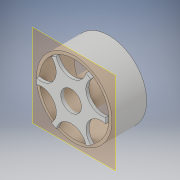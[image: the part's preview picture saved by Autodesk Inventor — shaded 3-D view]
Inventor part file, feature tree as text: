
AUTODESK INVENTOR PART (.ipt)
format: ipt  version: 2017 (Build 210142000, 142)  size: 158,720 bytes
history: native  units: in
note: dims shown in document units (in); Inventor stores cm internally (conversion verified against a paired STEP export)
features: extrude x3, sketch x3, projected_geometry x2, plane x1, pattern_circular x1
ambient origin geometry x8: Origin, YZ Plane, XZ Plane, XY Plane, X Axis, Y Axis, Z Axis, Center Point
bodies: Solid1 (feature_tree)
feature tree (10):
  extrude  "Extrusion1"  Depth=0.05in
  plane  "Work Plane1"
  extrude  "Extrusion2"  Depth=0.05in
  extrude  "Extrusion3"  TaperAngle=0.0deg  [1 undecoded]
  pattern_circular  "Circular Pattern1"  [2 undecoded]
  sketch  "Sketch1"  dims[d0=0.44in d1=0.05in]
  sketch  "Sketch2"  dims[d2=0.35in d3=0.05in]
  projected_geometry  "Projected Loop1"
  projected_geometry  "Projected Loop2"
  sketch  "Sketch3"  dims[d4=0.57in d5=0.0in d6=0.0in d7=0.05in d8=0.0in d9=0.5in d10=0.05in d11=0.0in d12=2.3622in d13=360.0deg]
note: 3 required parameter values undecoded (feature->parameter linkage not recoverable at this tier; creation-order binding heuristic only, values carry confidence <= 0.55)
